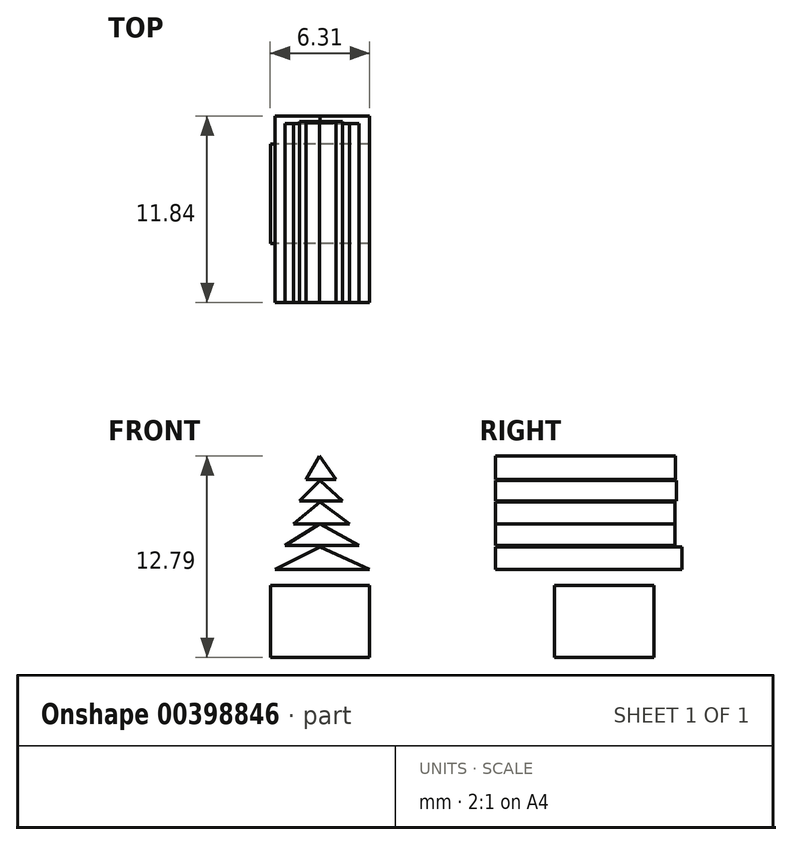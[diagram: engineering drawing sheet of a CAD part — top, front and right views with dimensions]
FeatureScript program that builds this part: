
annotation { "Feature Type Name" : "Feature", "Feature Type Description" : "" }
export const myFeature = defineFeature(function(context is Context, id is Id, definition is map)
    precondition{}
    {
        {
            var Q0;
            Q0=qCreatedBy(makeId("Top.planeOp"),FACE);
            var sketch = newSketch(context, id + "F0", { "sketchPlane" : qUnion([Q0])});
            skLineSegment(sketch, "E0.bottom", {"start": v(0, 3.74) * mm, "end": v(-6.3, 3.74) * mm});
            skLineSegment(sketch, "E0.top", {"start": v(0, 10.05) * mm, "end": v(-6.3, 10.05) * mm});
            skLineSegment(sketch, "E0.left", {"start": v(0, 3.74) * mm, "end": v(0, 10.05) * mm});
            skLineSegment(sketch, "E0.right", {"start": v(-6.3, 3.74) * mm, "end": v(-6.3, 10.05) * mm});
            skPoint(sketch, "E0.middle", {"position": v(-3.15, 6.9) * mm});
            skSolve(sketch);
        }
        {
            var Q0;
            Q0=makeQuery(id+"F0.imprint","IMPRINT",FACE,{"disambiguationData":[TD([[makeQuery(id+"F0.imprint","IMPRINT",EDGE,{"derivedFrom":sQuery(id+"F0.wireOp",EDGE,"E0.bottom")}),-1.0]])]});
            extrude(context, id + "F1", {"entities" : qUnion([Q0]), "depth" : 4.57 * mm});
        }
        {
            var Q0;
            Q0=qCreatedBy(makeId("Front.planeOp"),FACE);
            var sketch = newSketch(context, id + "F2", { "sketchPlane" : qUnion([Q0])});
            skLineSegment(sketch, "E1", {"start": v(-3.17, 12.8) * mm, "end": v(-4.04, 11.3) * mm});
            skLineSegment(sketch, "E2", {"start": v(-4.04, 11.3) * mm, "end": v(-2.12, 11.3) * mm});
            skLineSegment(sketch, "E3", {"start": v(-2.12, 11.3) * mm, "end": v(-3.17, 12.8) * mm});
            skSolve(sketch);
        }
        {
            var Q0;
            Q0=makeQuery(id+"F2.imprint","IMPRINT",FACE,{"disambiguationData":[TD([[makeQuery(id+"F2.imprint","IMPRINT",EDGE,{"derivedFrom":sQuery(id+"F2.wireOp",EDGE,"E1")}),1.0]])]});
            extrude(context, id + "F3", {"entities" : qUnion([Q0]), "oppositeDirection" : true, "depth" : 11.43 * mm});
        }
        {
            var Q0;
            Q0=qCreatedBy(makeId("Front.planeOp"),FACE);
            var sketch = newSketch(context, id + "F4", { "sketchPlane" : qUnion([Q0])});
            skLineSegment(sketch, "E4", {"start": v(-3.14, 11.23) * mm, "end": v(-4.44, 9.93) * mm});
            skLineSegment(sketch, "E5", {"start": v(-4.44, 9.93) * mm, "end": v(-1.74, 9.93) * mm});
            skLineSegment(sketch, "E6", {"start": v(-1.74, 9.93) * mm, "end": v(-3.14, 11.23) * mm});
            skSolve(sketch);
        }
        {
            var Q0;
            Q0=makeQuery(id+"F4.imprint","IMPRINT",FACE,{"disambiguationData":[TD([[makeQuery(id+"F4.imprint","IMPRINT",EDGE,{"derivedFrom":sQuery(id+"F4.wireOp",EDGE,"E4")}),1.0]])]});
            extrude(context, id + "F5", {"entities" : qUnion([Q0]), "oppositeDirection" : true, "depth" : 11.48 * mm});
        }
        {
            var Q0;
            Q0=qCreatedBy(makeId("Front.planeOp"),FACE);
            var sketch = newSketch(context, id + "F6", { "sketchPlane" : qUnion([Q0])});
            skLineSegment(sketch, "E7", {"start": v(-3.15, 9.87) * mm, "end": v(-4.84, 8.48) * mm});
            skLineSegment(sketch, "E8", {"start": v(-4.84, 8.48) * mm, "end": v(-1.27, 8.48) * mm});
            skLineSegment(sketch, "E9", {"start": v(-1.27, 8.48) * mm, "end": v(-3.15, 9.87) * mm});
            skSolve(sketch);
        }
        {
            var Q0;
            Q0=makeQuery(id+"F6.imprint","IMPRINT",FACE,{"disambiguationData":[TD([[makeQuery(id+"F6.imprint","IMPRINT",EDGE,{"derivedFrom":sQuery(id+"F6.wireOp",EDGE,"E7")}),1.0]])]});
            extrude(context, id + "F7", {"entities" : qUnion([Q0]), "oppositeDirection" : true, "depth" : 11.38 * mm});
        }
        {
            var Q0;
            Q0=qCreatedBy(makeId("Front.planeOp"),FACE);
            var sketch = newSketch(context, id + "F8", { "sketchPlane" : qUnion([Q0])});
            skLineSegment(sketch, "E10", {"start": v(-3.17, 8.5) * mm, "end": v(-5.38, 7.1) * mm});
            skLineSegment(sketch, "E11", {"start": v(-5.38, 7.1) * mm, "end": v(-0.68, 7.1) * mm});
            skLineSegment(sketch, "E12", {"start": v(-0.68, 7.1) * mm, "end": v(-3.17, 8.5) * mm});
            skSolve(sketch);
        }
        {
            var Q0;
            Q0=makeQuery(id+"F8.imprint","IMPRINT",FACE,{"disambiguationData":[TD([[makeQuery(id+"F8.imprint","IMPRINT",EDGE,{"derivedFrom":sQuery(id+"F8.wireOp",EDGE,"E10")}),1.0]])]});
            extrude(context, id + "F9", {"entities" : qUnion([Q0]), "operationType" : NewBodyOperationType.ADD, "oppositeDirection" : true, "depth" : 11.38 * mm});
        }
        {
            var Q0;
            Q0=qCreatedBy(makeId("Front.planeOp"),FACE);
            var sketch = newSketch(context, id + "F10", { "sketchPlane" : qUnion([Q0])});
            skLineSegment(sketch, "E13", {"start": v(-3.15, 7.03) * mm, "end": v(-6, 5.6) * mm});
            skLineSegment(sketch, "E14", {"start": v(-6, 5.6) * mm, "end": v(0, 5.6) * mm});
            skLineSegment(sketch, "E15", {"start": v(0, 5.6) * mm, "end": v(-3.15, 7.03) * mm});
            skSolve(sketch);
        }
        {
            var Q0;
            Q0=makeQuery(id+"F10.imprint","IMPRINT",FACE,{"disambiguationData":[TD([[makeQuery(id+"F10.imprint","IMPRINT",EDGE,{"derivedFrom":sQuery(id+"F10.wireOp",EDGE,"E13")}),1.0]])]});
            extrude(context, id + "F11", {"entities" : qUnion([Q0]), "oppositeDirection" : true, "depth" : 11.84 * mm});
        }
    });
